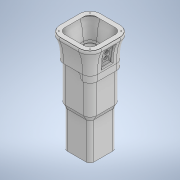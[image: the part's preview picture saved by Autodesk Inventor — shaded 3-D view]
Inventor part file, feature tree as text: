
AUTODESK INVENTOR PART (.ipt)
format: ipt  version: 2021 (Build 250183000, 183)  size: 1,038,336 bytes
history: native  units: mm
features: sketch x18, extrude x10, projected_geometry x9, other x4, plane x3, chamfer x3, fillet x3, hole x3, loft x2, shell x1, sweep x1
ambient origin geometry x8: Origin, YZ Plane, XZ Plane, XY Plane, X Axis, Y Axis, Z Axis, Center Point
bodies: Body1 (feature_tree), Body2 (feature_tree), Body3 (feature_tree)
feature tree (57):
  other  "實體1"
  sketch  "草圖1"
  plane  "工作平面1"
  sketch  "草圖2"
  extrude  "擠出1"  Depth=174.0mm
  loft  "斷面混成1"
  extrude  "擠出2"  Depth=25.0mm
  plane  "工作平面2"
  extrude  "擠出6"  Depth=30.0mm
  loft  "斷面混成3"
  chamfer  "倒角2"  Distance=205.0mm
  fillet  "圓角3"  Radius=45.0mm
  extrude  "擠出7"  Depth=240.0mm TaperAngle=0.0deg
  fillet  "圓角4"  [1 undecoded]
  shell  "薄殼2"  Thickness=0.0mm
  chamfer  "倒角1"  Distance=400.0mm
  extrude  "擠出9"  [1 undecoded]
  chamfer  "倒角4"  Distance=225.0mm
  hole  "孔4"  [1 undecoded]
  sweep  "掃掠3"
  hole  "孔6"  [1 undecoded]
  extrude  "擠出10"  Depth=30.0mm
  plane  "工作平面3"
  extrude  "擠出11"  Depth=10.0mm TaperAngle=75.0deg
  fillet  "圓角5"  Radius=20.0mm
  hole  "孔7"  [1 undecoded]
  extrude  "擠出13"  Depth=50.0mm
  extrude  "擠出14"  Depth=40.0mm TaperAngle=0.0deg
  extrude  "擠出12"  Depth=20.0mm
  sketch  "草圖3"
  projected_geometry  "投影迴路1"
  sketch  "草圖17"
  sketch  "草圖18"
  projected_geometry  "投影迴路7"
  sketch  "草圖20"
  projected_geometry  "投影迴路9"
  sketch  "草圖23"
  projected_geometry  "投影迴路10"
  sketch  "草圖24"
  sketch  "草圖25"
  sketch  "3D 草圖2"
  sketch  "草圖27"
  sketch  "草圖28"
  other  "Srf1"
  sketch  "草圖29"
  sketch  "草圖30"
  projected_geometry  "投影迴路11"
  sketch  "草圖31"
  projected_geometry  "投影迴路12"
  sketch  "草圖32"
  projected_geometry  "投影迴路13"
  sketch  "草圖33"
  projected_geometry  "投影迴路14"
  sketch  "草圖34"
  projected_geometry  "投影迴路15"
  other  "擠出表面1"
  other  "投影切割邊5"
note: 5 required parameter values undecoded (feature->parameter linkage not recoverable at this tier; creation-order binding heuristic only, values carry confidence <= 0.55)
